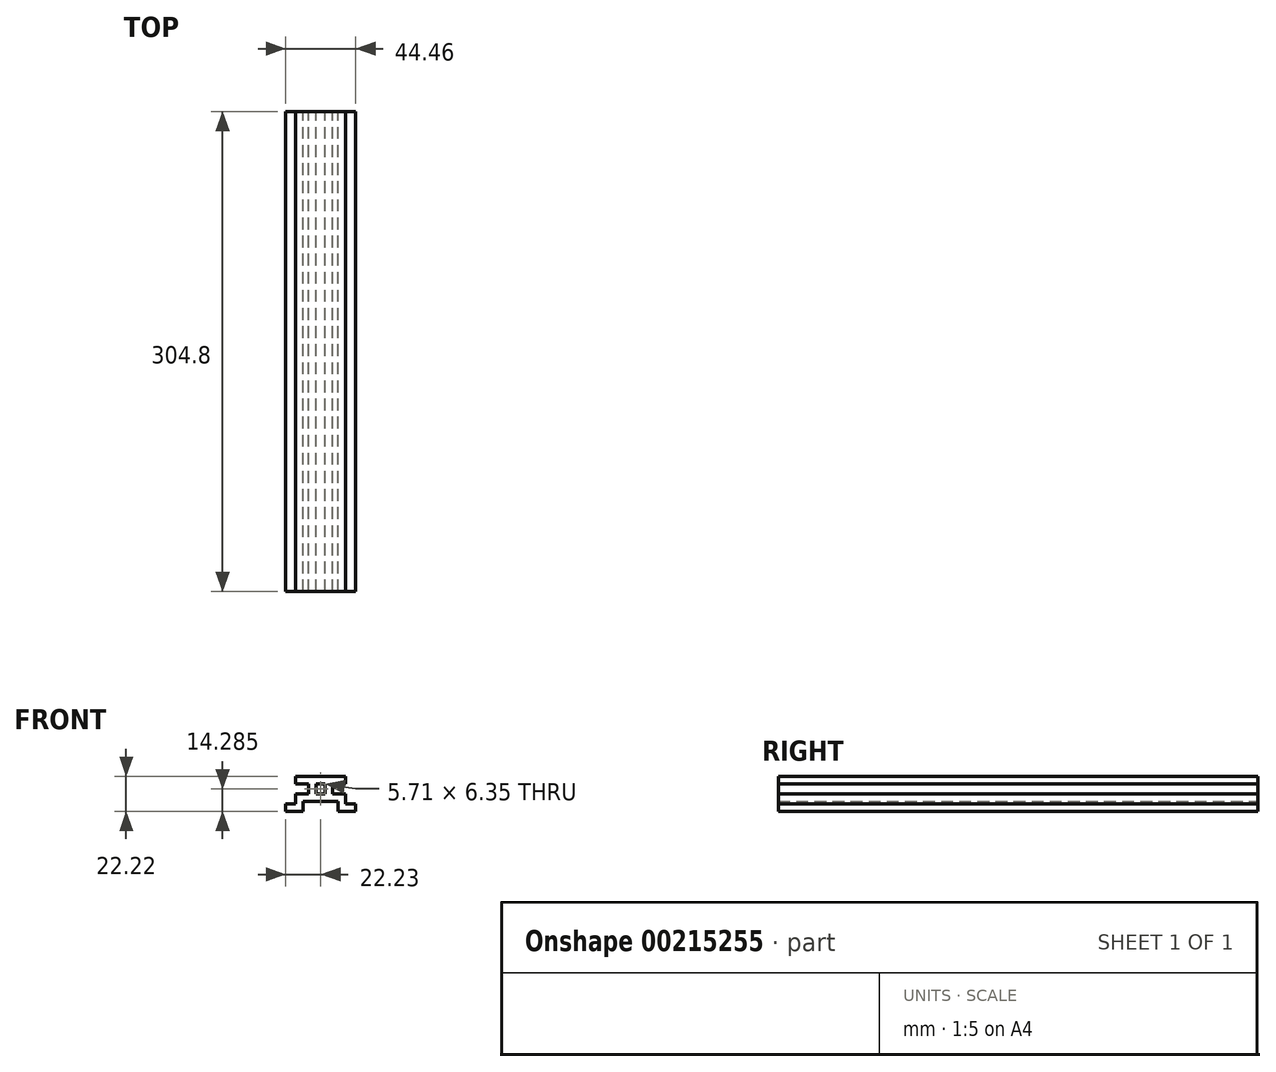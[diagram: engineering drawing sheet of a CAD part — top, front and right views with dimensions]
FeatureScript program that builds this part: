
annotation { "Feature Type Name" : "Feature", "Feature Type Description" : "" }
export const myFeature = defineFeature(function(context is Context, id is Id, definition is map)
    precondition{}
    {
        {
            var Q0;
            Q0=qCreatedBy(makeId("Front.planeOp"),FACE);
            var sketch = newSketch(context, id + "F0", { "sketchPlane" : qUnion([Q0])});
            skLineSegment(sketch, "E0", {"start": v(0, 30.35) * mm, "end": v(0, 11.11) * mm, "construction": true});
            skLineSegment(sketch, "E1", {"start": v(-22.22, -6.35) * mm, "end": v(-15.88, -6.35) * mm});
            skLineSegment(sketch, "E2", {"start": v(-15.88, -6.35) * mm, "end": v(-15.88, 0) * mm});
            skLineSegment(sketch, "E3", {"start": v(-15.88, 0) * mm, "end": v(-7.62, 0) * mm});
            skLineSegment(sketch, "E4", {"start": v(-7.62, 0) * mm, "end": v(-7.62, 6.35) * mm});
            skLineSegment(sketch, "E5", {"start": v(-7.62, 6.35) * mm, "end": v(-15.88, 6.35) * mm});
            skLineSegment(sketch, "E6.0", {"start": v(0, 11.11) * mm, "end": v(-15.88, 11.11) * mm});
            skLineSegment(sketch, "E6.1", {"start": v(-22.22, -11.11) * mm, "end": v(-11.11, -11.11) * mm});
            skLineSegment(sketch, "E6.2", {"start": v(-11.11, -11.11) * mm, "end": v(-11.11, -4.76) * mm});
            skLineSegment(sketch, "E6.3", {"start": v(-11.11, -4.76) * mm, "end": v(0, -4.76) * mm});
            skLineSegment(sketch, "E6.4", {"start": v(-2.86, 0) * mm, "end": v(-2.86, 6.35) * mm});
            skLineSegment(sketch, "E7", {"start": v(-15.88, 11.11) * mm, "end": v(-15.88, 6.35) * mm});
            skLineSegment(sketch, "E8", {"start": v(-22.22, -6.35) * mm, "end": v(-22.22, -11.11) * mm});
            skLineSegment(sketch, "E9", {"start": v(-2.86, 6.35) * mm, "end": v(0, 6.35) * mm});
            skLineSegment(sketch, "E10", {"start": v(-2.86, 0) * mm, "end": v(0, 0) * mm});
            skLineSegment(sketch, "E11.MirrorCS", {"start": v(22.22, -6.35) * mm, "end": v(22.22, -11.11) * mm});
            skLineSegment(sketch, "E12.MirrorCS", {"start": v(15.88, 11.11) * mm, "end": v(15.88, 6.35) * mm});
            skLineSegment(sketch, "E13.MirrorCS", {"start": v(2.86, 0) * mm, "end": v(0, 0) * mm});
            skLineSegment(sketch, "E14.MirrorCS", {"start": v(2.86, 6.35) * mm, "end": v(0, 6.35) * mm});
            skLineSegment(sketch, "E15.MirrorCS", {"start": v(2.86, 0) * mm, "end": v(2.86, 6.35) * mm});
            skLineSegment(sketch, "E16.MirrorCS", {"start": v(11.11, -4.76) * mm, "end": v(0, -4.76) * mm});
            skLineSegment(sketch, "E17.MirrorCS", {"start": v(11.11, -11.11) * mm, "end": v(11.11, -4.76) * mm});
            skLineSegment(sketch, "E18.MirrorCS", {"start": v(22.22, -11.11) * mm, "end": v(11.11, -11.11) * mm});
            skLineSegment(sketch, "E19.MirrorCS", {"start": v(0, 11.11) * mm, "end": v(15.88, 11.11) * mm});
            skLineSegment(sketch, "E20.MirrorCS", {"start": v(7.62, 6.35) * mm, "end": v(15.88, 6.35) * mm});
            skLineSegment(sketch, "E21.MirrorCS", {"start": v(7.62, 0) * mm, "end": v(7.62, 6.35) * mm});
            skLineSegment(sketch, "E22.MirrorCS", {"start": v(15.88, 0) * mm, "end": v(7.62, 0) * mm});
            skLineSegment(sketch, "E23.MirrorCS", {"start": v(15.88, -6.35) * mm, "end": v(15.88, 0) * mm});
            skLineSegment(sketch, "E24.MirrorCS", {"start": v(22.22, -6.35) * mm, "end": v(15.88, -6.35) * mm});
            skLineSegment(sketch, "E25.trimOffspring", {"start": v(0, 6.35) * mm, "end": v(0, 0) * mm, "construction": true});
            skLineSegment(sketch, "E26.trimOffspring", {"start": v(0, -4.76) * mm, "end": v(0, -34.7) * mm, "construction": true});
            skSolve(sketch);
        }
        {
            var Q0;
            Q0=makeQuery(id+"F0.imprint","IMPRINT",FACE,{"disambiguationData":[TD([[makeQuery(id+"F0.imprint","IMPRINT",EDGE,{"derivedFrom":sQuery(id+"F0.wireOp",EDGE,"E1")}),-1.0]])]});
            extrude(context, id + "F1", {"entities" : qUnion([Q0]), "depth" : 304.8 * mm});
        }
    });
